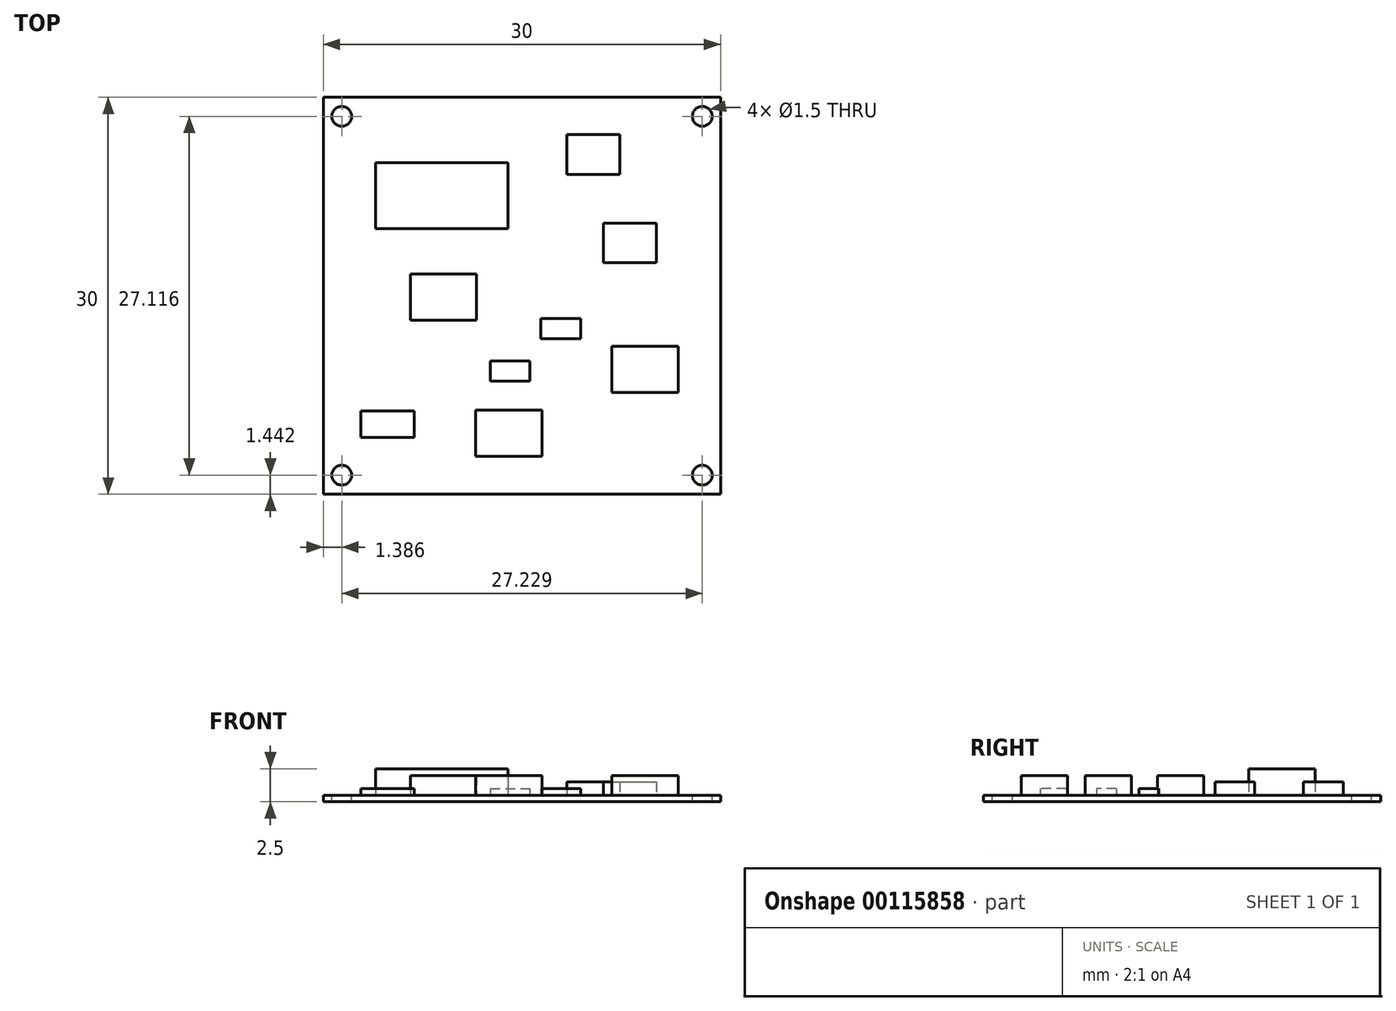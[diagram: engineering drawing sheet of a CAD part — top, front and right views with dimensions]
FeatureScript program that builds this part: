
annotation { "Feature Type Name" : "Feature", "Feature Type Description" : "" }
export const myFeature = defineFeature(function(context is Context, id is Id, definition is map)
    precondition{}
    {
        {
            var Q0;
            Q0=qCreatedBy(makeId("Top.planeOp"),FACE);
            var sketch = newSketch(context, id + "F0", { "sketchPlane" : qUnion([Q0])});
            skLineSegment(sketch, "E0.top", {"start": v(0, 15) * mm, "end": v(15, 15) * mm});
            skLineSegment(sketch, "E0.right", {"start": v(15, 0) * mm, "end": v(15, 15) * mm});
            skLineSegment(sketch, "E1.top", {"start": v(0, 15) * mm, "end": v(-15, 15) * mm});
            skLineSegment(sketch, "E1.right", {"start": v(-15, 0) * mm, "end": v(-15, 15) * mm});
            skLineSegment(sketch, "E2.top", {"start": v(-15, -15) * mm, "end": v(15, -15) * mm});
            skLineSegment(sketch, "E2.left", {"start": v(-15, 0) * mm, "end": v(-15, -15) * mm});
            skLineSegment(sketch, "E2.right", {"start": v(15, 0) * mm, "end": v(15, -15) * mm});
            skLineSegment(sketch, "E3.bottom", {"start": v(-11.06, 10.06) * mm, "end": v(-1.06, 10.06) * mm});
            skLineSegment(sketch, "E3.top", {"start": v(-11.06, 5.06) * mm, "end": v(-1.06, 5.06) * mm});
            skLineSegment(sketch, "E3.left", {"start": v(-11.06, 10.06) * mm, "end": v(-11.06, 5.06) * mm});
            skLineSegment(sketch, "E3.right", {"start": v(-1.06, 10.06) * mm, "end": v(-1.06, 5.06) * mm});
            skLineSegment(sketch, "E4.bottom", {"start": v(-8.43, 1.66) * mm, "end": v(-3.43, 1.66) * mm});
            skLineSegment(sketch, "E4.top", {"start": v(-8.43, -1.84) * mm, "end": v(-3.43, -1.84) * mm});
            skLineSegment(sketch, "E4.left", {"start": v(-8.43, 1.66) * mm, "end": v(-8.43, -1.84) * mm});
            skLineSegment(sketch, "E4.right", {"start": v(-3.43, 1.66) * mm, "end": v(-3.43, -1.84) * mm});
            skLineSegment(sketch, "E5.bottom", {"start": v(-3.5, -8.64) * mm, "end": v(1.5, -8.64) * mm});
            skLineSegment(sketch, "E5.top", {"start": v(-3.5, -12.14) * mm, "end": v(1.5, -12.14) * mm});
            skLineSegment(sketch, "E5.left", {"start": v(-3.5, -8.64) * mm, "end": v(-3.5, -12.14) * mm});
            skLineSegment(sketch, "E5.right", {"start": v(1.5, -8.64) * mm, "end": v(1.5, -12.14) * mm});
            skLineSegment(sketch, "E6.bottom", {"start": v(6.8, -3.82) * mm, "end": v(11.8, -3.82) * mm});
            skLineSegment(sketch, "E6.top", {"start": v(6.8, -7.32) * mm, "end": v(11.8, -7.32) * mm});
            skLineSegment(sketch, "E6.left", {"start": v(6.8, -3.82) * mm, "end": v(6.8, -7.32) * mm});
            skLineSegment(sketch, "E6.right", {"start": v(11.8, -3.82) * mm, "end": v(11.8, -7.32) * mm});
            skLineSegment(sketch, "E7.bottom", {"start": v(1.43, -1.73) * mm, "end": v(4.43, -1.73) * mm});
            skLineSegment(sketch, "E7.top", {"start": v(1.43, -3.23) * mm, "end": v(4.43, -3.23) * mm});
            skLineSegment(sketch, "E7.left", {"start": v(1.43, -1.73) * mm, "end": v(1.43, -3.23) * mm});
            skLineSegment(sketch, "E7.right", {"start": v(4.43, -1.73) * mm, "end": v(4.43, -3.23) * mm});
            skLineSegment(sketch, "E8.bottom", {"start": v(-2.4, -4.94) * mm, "end": v(0.6, -4.94) * mm});
            skLineSegment(sketch, "E8.top", {"start": v(-2.4, -6.44) * mm, "end": v(0.6, -6.44) * mm});
            skLineSegment(sketch, "E8.left", {"start": v(-2.4, -4.94) * mm, "end": v(-2.4, -6.44) * mm});
            skLineSegment(sketch, "E8.right", {"start": v(0.6, -4.94) * mm, "end": v(0.6, -6.44) * mm});
            skLineSegment(sketch, "E9.bottom", {"start": v(6.14, 5.5) * mm, "end": v(10.14, 5.5) * mm});
            skLineSegment(sketch, "E9.top", {"start": v(6.14, 2.5) * mm, "end": v(10.14, 2.5) * mm});
            skLineSegment(sketch, "E9.left", {"start": v(6.14, 5.5) * mm, "end": v(6.14, 2.5) * mm});
            skLineSegment(sketch, "E9.right", {"start": v(10.14, 5.5) * mm, "end": v(10.14, 2.5) * mm});
            skLineSegment(sketch, "E10.bottom", {"start": v(3.4, 12.18) * mm, "end": v(7.4, 12.18) * mm});
            skLineSegment(sketch, "E10.top", {"start": v(3.4, 9.18) * mm, "end": v(7.4, 9.18) * mm});
            skLineSegment(sketch, "E10.left", {"start": v(3.4, 12.18) * mm, "end": v(3.4, 9.18) * mm});
            skLineSegment(sketch, "E10.right", {"start": v(7.4, 12.18) * mm, "end": v(7.4, 9.18) * mm});
            skLineSegment(sketch, "E11.bottom", {"start": v(-12.15, -8.72) * mm, "end": v(-8.15, -8.72) * mm});
            skLineSegment(sketch, "E11.top", {"start": v(-12.15, -10.72) * mm, "end": v(-8.15, -10.72) * mm});
            skLineSegment(sketch, "E11.left", {"start": v(-12.15, -8.72) * mm, "end": v(-12.15, -10.72) * mm});
            skLineSegment(sketch, "E11.right", {"start": v(-8.15, -8.72) * mm, "end": v(-8.15, -10.72) * mm});
            skCircle(sketch, "E12", {"center": v(-13.61, 13.56) * mm, "radius": 0.75 * mm});
            skSolve(sketch);
        }
        {
            var Q0;
            Q0=makeQuery(id+"F0.imprint","IMPRINT",FACE,{"disambiguationData":[TD([[makeQuery(id+"F0.imprint","IMPRINT",EDGE,{"derivedFrom":sQuery(id+"F0.wireOp",EDGE,"E0.top")}),-1.0]])]});
            var Q1;
            Q1=makeQuery(id+"F0.imprint","IMPRINT",FACE,{"disambiguationData":[TD([[makeQuery(id+"F0.imprint","IMPRINT",EDGE,{"derivedFrom":sQuery(id+"F0.wireOp",EDGE,"E3.bottom")}),-1.0]])]});
            var Q2;
            Q2=makeQuery(id+"F0.imprint","IMPRINT",FACE,{"disambiguationData":[TD([[makeQuery(id+"F0.imprint","IMPRINT",EDGE,{"derivedFrom":sQuery(id+"F0.wireOp",EDGE,"E4.bottom")}),-1.0]])]});
            var Q3;
            Q3=makeQuery(id+"F0.imprint","IMPRINT",FACE,{"disambiguationData":[TD([[makeQuery(id+"F0.imprint","IMPRINT",EDGE,{"derivedFrom":sQuery(id+"F0.wireOp",EDGE,"E11.bottom")}),-1.0]])]});
            var Q4;
            Q4=makeQuery(id+"F0.imprint","IMPRINT",FACE,{"disambiguationData":[TD([[makeQuery(id+"F0.imprint","IMPRINT",EDGE,{"derivedFrom":sQuery(id+"F0.wireOp",EDGE,"E5.bottom")}),-1.0]])]});
            var Q5;
            Q5=makeQuery(id+"F0.imprint","IMPRINT",FACE,{"disambiguationData":[TD([[makeQuery(id+"F0.imprint","IMPRINT",EDGE,{"derivedFrom":sQuery(id+"F0.wireOp",EDGE,"E8.bottom")}),-1.0]])]});
            var Q6;
            Q6=makeQuery(id+"F0.imprint","IMPRINT",FACE,{"disambiguationData":[TD([[makeQuery(id+"F0.imprint","IMPRINT",EDGE,{"derivedFrom":sQuery(id+"F0.wireOp",EDGE,"E7.bottom")}),-1.0]])]});
            var Q7;
            Q7=makeQuery(id+"F0.imprint","IMPRINT",FACE,{"disambiguationData":[TD([[makeQuery(id+"F0.imprint","IMPRINT",EDGE,{"derivedFrom":sQuery(id+"F0.wireOp",EDGE,"E6.bottom")}),-1.0]])]});
            var Q8;
            Q8=makeQuery(id+"F0.imprint","IMPRINT",FACE,{"disambiguationData":[TD([[makeQuery(id+"F0.imprint","IMPRINT",EDGE,{"derivedFrom":sQuery(id+"F0.wireOp",EDGE,"E9.bottom")}),-1.0]])]});
            var Q9;
            Q9=makeQuery(id+"F0.imprint","IMPRINT",FACE,{"disambiguationData":[TD([[makeQuery(id+"F0.imprint","IMPRINT",EDGE,{"derivedFrom":sQuery(id+"F0.wireOp",EDGE,"E10.bottom")}),-1.0]])]});
            extrude(context, id + "F1", {"entities" : qUnion([Q0, Q1, Q2, Q3, Q4, Q5, Q6, Q7, Q8, Q9]), "oppositeDirection" : true, "depth" : 0.5 * mm});
        }
        {
            var Q0;
            Q0=makeQuery(id+"F0.imprint","IMPRINT",FACE,{"disambiguationData":[TD([[makeQuery(id+"F0.imprint","IMPRINT",EDGE,{"derivedFrom":sQuery(id+"F0.wireOp",EDGE,"E12")}),1.0]])]});
            var Q1;
            Q1=sQuery(id+"F0.wireOp",EDGE,"E12");
            var Q2;
            Q2=makeQuery(id+"F1.opExtrude","CAP_FACE",FACE,{"disambiguationData":[OSD([sQuery(id+"F0.wireOp",EDGE,"E0.top"),sQuery(id+"F0.wireOp",EDGE,"E0.right"),sQuery(id+"F0.wireOp",EDGE,"E1.top"),sQuery(id+"F0.wireOp",EDGE,"E1.right"),sQuery(id+"F0.wireOp",EDGE,"E2.top"),sQuery(id+"F0.wireOp",EDGE,"E2.left"),sQuery(id+"F0.wireOp",EDGE,"E2.right"),sQuery(id+"F0.wireOp",EDGE,"E12")])],"isStart":false});
            extrude(context, id + "F2", {"entities" : qUnion([Q0]), "surfaceEntities" : qUnion([Q1]), "endBound" : BoundingType.UP_TO_SURFACE, "oppositeDirection" : true, "endBoundEntityFace" : qUnion([Q2]), "depth" : 25 * mm});
        }
        {
            var Q0;
            Q0=makeQuery(id+"F2.opExtrude","SWEPT_BODY",BODY,{"disambiguationData":[OSD([sQuery(id+"F0.wireOp",EDGE,"E12")])]});
            var Q1;
            Q1=qCreatedBy(makeId("Front.planeOp"),FACE);
            mirror(context, id + "F3", {"entities" : qUnion([Q0]), "mirrorPlane" : qUnion([Q1])});
        }
        {
            var Q0;
            Q0=makeQuery(id+"F2.opExtrude","SWEPT_BODY",BODY,{"disambiguationData":[OSD([sQuery(id+"F0.wireOp",EDGE,"E12")])]});
            var Q1;
            Q1=makeQuery(id+"F3.opPattern","COPY",BODY,{"derivedFrom":makeQuery(id+"F2.opExtrude","SWEPT_BODY",BODY,{"disambiguationData":[OSD([sQuery(id+"F0.wireOp",EDGE,"E12")])]}),"instanceName":"1"});
            var Q2;
            Q2=qCreatedBy(makeId("Right.planeOp"),FACE);
            mirror(context, id + "F4", {"entities" : qUnion([Q0, Q1]), "mirrorPlane" : qUnion([Q2])});
        }
        {
            var Q0;
            Q0=makeQuery(id+"F3.opPattern","COPY",BODY,{"derivedFrom":makeQuery(id+"F2.opExtrude","SWEPT_BODY",BODY,{"disambiguationData":[OSD([sQuery(id+"F0.wireOp",EDGE,"E12")])]}),"instanceName":"1"});
            var Q1;
            Q1=makeQuery(id+"F4.opPattern","COPY",BODY,{"derivedFrom":makeQuery(id+"F2.opExtrude","SWEPT_BODY",BODY,{"disambiguationData":[OSD([sQuery(id+"F0.wireOp",EDGE,"E12")])]}),"instanceName":"1"});
            var Q2;
            Q2=makeQuery(id+"F4.opPattern","COPY",BODY,{"derivedFrom":makeQuery(id+"F3.opPattern","COPY",BODY,{"derivedFrom":makeQuery(id+"F2.opExtrude","SWEPT_BODY",BODY,{"disambiguationData":[OSD([sQuery(id+"F0.wireOp",EDGE,"E12")])]}),"instanceName":"1"}),"instanceName":"1"});
            var Q3;
            Q3=makeQuery(id+"F1.opExtrude","SWEPT_BODY",BODY,{"disambiguationData":[OSD([sQuery(id+"F0.wireOp",EDGE,"E0.top"),sQuery(id+"F0.wireOp",EDGE,"E0.right"),sQuery(id+"F0.wireOp",EDGE,"E1.top"),sQuery(id+"F0.wireOp",EDGE,"E1.right"),sQuery(id+"F0.wireOp",EDGE,"E2.top"),sQuery(id+"F0.wireOp",EDGE,"E2.left"),sQuery(id+"F0.wireOp",EDGE,"E2.right"),sQuery(id+"F0.wireOp",EDGE,"E12")])]});
            booleanBodies(context, id + "F5", {"operationType" : BooleanOperationType.SUBTRACTION, "tools" : qUnion([Q0, Q1, Q2]), "targets" : qUnion([Q3])});
        }
        {
            var Q0;
            Q0=makeQuery(id+"F2.opExtrude","SWEPT_BODY",BODY,{"disambiguationData":[OSD([sQuery(id+"F0.wireOp",EDGE,"E12")])]});
            deleteBodies(context, id + "F6", {"entities" : qUnion([Q0])});
        }
        {
            var Q0;
            Q0=makeQuery(id+"F0.imprint","IMPRINT",FACE,{"disambiguationData":[TD([[makeQuery(id+"F0.imprint","IMPRINT",EDGE,{"derivedFrom":sQuery(id+"F0.wireOp",EDGE,"E3.bottom")}),-1.0]])]});
            extrude(context, id + "F7", {"entities" : qUnion([Q0]), "depth" : 2 * mm});
        }
        {
            var Q0;
            Q0=makeQuery(id+"F0.imprint","IMPRINT",FACE,{"disambiguationData":[TD([[makeQuery(id+"F0.imprint","IMPRINT",EDGE,{"derivedFrom":sQuery(id+"F0.wireOp",EDGE,"E4.bottom")}),-1.0]])]});
            var Q1;
            Q1=makeQuery(id+"F0.imprint","IMPRINT",FACE,{"disambiguationData":[TD([[makeQuery(id+"F0.imprint","IMPRINT",EDGE,{"derivedFrom":sQuery(id+"F0.wireOp",EDGE,"E5.bottom")}),-1.0]])]});
            var Q2;
            Q2=makeQuery(id+"F0.imprint","IMPRINT",FACE,{"disambiguationData":[TD([[makeQuery(id+"F0.imprint","IMPRINT",EDGE,{"derivedFrom":sQuery(id+"F0.wireOp",EDGE,"E6.bottom")}),-1.0]])]});
            extrude(context, id + "F8", {"entities" : qUnion([Q0, Q1, Q2]), "depth" : 1.5 * mm});
        }
        {
            var Q0;
            Q0=makeQuery(id+"F0.imprint","IMPRINT",FACE,{"disambiguationData":[TD([[makeQuery(id+"F0.imprint","IMPRINT",EDGE,{"derivedFrom":sQuery(id+"F0.wireOp",EDGE,"E9.bottom")}),-1.0]])]});
            var Q1;
            Q1=makeQuery(id+"F0.imprint","IMPRINT",FACE,{"disambiguationData":[TD([[makeQuery(id+"F0.imprint","IMPRINT",EDGE,{"derivedFrom":sQuery(id+"F0.wireOp",EDGE,"E10.bottom")}),-1.0]])]});
            extrude(context, id + "F9", {"entities" : qUnion([Q0, Q1]), "depth" : 1 * mm});
        }
        {
            var Q0;
            Q0=makeQuery(id+"F0.imprint","IMPRINT",FACE,{"disambiguationData":[TD([[makeQuery(id+"F0.imprint","IMPRINT",EDGE,{"derivedFrom":sQuery(id+"F0.wireOp",EDGE,"E8.bottom")}),-1.0]])]});
            var Q1;
            Q1=makeQuery(id+"F0.imprint","IMPRINT",FACE,{"disambiguationData":[TD([[makeQuery(id+"F0.imprint","IMPRINT",EDGE,{"derivedFrom":sQuery(id+"F0.wireOp",EDGE,"E7.bottom")}),-1.0]])]});
            var Q2;
            Q2=makeQuery(id+"F0.imprint","IMPRINT",FACE,{"disambiguationData":[TD([[makeQuery(id+"F0.imprint","IMPRINT",EDGE,{"derivedFrom":sQuery(id+"F0.wireOp",EDGE,"E11.bottom")}),-1.0]])]});
            extrude(context, id + "F10", {"entities" : qUnion([Q0, Q1, Q2]), "depth" : 0.5 * mm});
        }
        {
            var Q0;
            Q0=sQuery(id+"F0.wireOp",EDGE,"E3.bottom");
            var Q1;
            Q1=sQuery(id+"F0.wireOp",EDGE,"E3.left");
            var Q2;
            Q2=sQuery(id+"F0.wireOp",EDGE,"E3.top");
            var Q3;
            Q3=sQuery(id+"F0.wireOp",EDGE,"E3.right");
            var Q4;
            Q4=sQuery(id+"F0.wireOp",EDGE,"E10.left");
            var Q5;
            Q5=sQuery(id+"F0.wireOp",EDGE,"E10.bottom");
            var Q6;
            Q6=sQuery(id+"F0.wireOp",EDGE,"E10.right");
            var Q7;
            Q7=sQuery(id+"F0.wireOp",EDGE,"E10.top");
            var Q8;
            Q8=sQuery(id+"F0.wireOp",EDGE,"E9.left");
            var Q9;
            Q9=sQuery(id+"F0.wireOp",EDGE,"E9.bottom");
            var Q10;
            Q10=sQuery(id+"F0.wireOp",EDGE,"E9.right");
            var Q11;
            Q11=sQuery(id+"F0.wireOp",EDGE,"E9.top");
            var Q12;
            Q12=sQuery(id+"F0.wireOp",EDGE,"E6.bottom");
            var Q13;
            Q13=sQuery(id+"F0.wireOp",EDGE,"E6.left");
            var Q14;
            Q14=sQuery(id+"F0.wireOp",EDGE,"E6.top");
            var Q15;
            Q15=sQuery(id+"F0.wireOp",EDGE,"E6.right");
            var Q16;
            Q16=sQuery(id+"F0.wireOp",EDGE,"E7.bottom");
            var Q17;
            Q17=sQuery(id+"F0.wireOp",EDGE,"E7.top");
            var Q18;
            Q18=sQuery(id+"F0.wireOp",EDGE,"E7.left");
            var Q19;
            Q19=sQuery(id+"F0.wireOp",EDGE,"E7.right");
            var Q20;
            Q20=sQuery(id+"F0.wireOp",EDGE,"E8.bottom");
            var Q21;
            Q21=sQuery(id+"F0.wireOp",EDGE,"E8.top");
            var Q22;
            Q22=sQuery(id+"F0.wireOp",EDGE,"E8.right");
            var Q23;
            Q23=sQuery(id+"F0.wireOp",EDGE,"E8.left");
            var Q24;
            Q24=sQuery(id+"F0.wireOp",EDGE,"E4.right");
            var Q25;
            Q25=sQuery(id+"F0.wireOp",EDGE,"E4.bottom");
            var Q26;
            Q26=sQuery(id+"F0.wireOp",EDGE,"E4.top");
            var Q27;
            Q27=sQuery(id+"F0.wireOp",EDGE,"E4.left");
            var Q28;
            Q28=sQuery(id+"F0.wireOp",EDGE,"E11.bottom");
            var Q29;
            Q29=sQuery(id+"F0.wireOp",EDGE,"E11.top");
            var Q30;
            Q30=sQuery(id+"F0.wireOp",EDGE,"E11.left");
            var Q31;
            Q31=sQuery(id+"F0.wireOp",EDGE,"E11.right");
            var Q32;
            Q32=sQuery(id+"F0.wireOp",EDGE,"E5.left");
            var Q33;
            Q33=sQuery(id+"F0.wireOp",EDGE,"E5.bottom");
            var Q34;
            Q34=sQuery(id+"F0.wireOp",EDGE,"E5.top");
            var Q35;
            Q35=sQuery(id+"F0.wireOp",EDGE,"E5.right");
            extrude(context, id + "F11", {"bodyType" : ToolBodyType.SURFACE, "surfaceEntities" : qUnion([Q0, Q1, Q2, Q3, Q4, Q5, Q6, Q7, Q8, Q9, Q10, Q11, Q12, Q13, Q14, Q15, Q16, Q17, Q18, Q19, Q20, Q21, Q22, Q23, Q24, Q25, Q26, Q27, Q28, Q29, Q30, Q31, Q32, Q33, Q34, Q35]), "endBound" : BoundingType.SYMMETRIC, "oppositeDirection" : true, "depth" : 3 * mm});
        }
    });
